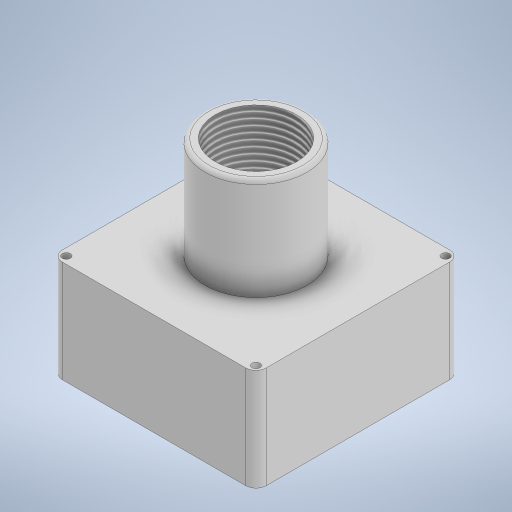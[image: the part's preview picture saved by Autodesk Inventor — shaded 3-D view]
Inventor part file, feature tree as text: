
AUTODESK INVENTOR PART (.ipt)
format: ipt  version: 2024 (Build 280153000, 153)  size: 256,512 bytes
history: native  units: in
note: dims shown in document units (in); Inventor stores cm internally (conversion verified against a paired STEP export)
features: extrude x3, sketch x3, thread x1, fillet x1
ambient origin geometry x8: Origin, YZ Plane, XZ Plane, XY Plane, X Axis, Y Axis, Z Axis, Center Point
bodies: Solid1 (feature_tree)
feature tree (8):
  extrude  "Extrusion1"  Depth=3.937in
  extrude  "Extrusion2"  Depth=1.9685in TaperAngle=0.0deg
  extrude  "Extrusion3"  Depth=1.1811in TaperAngle=0.0deg
  thread  "Thread1"  [1 undecoded]
  fillet  "Fillet1"  Radius=0.0787in
  sketch  "Sketch1"  dims[d0=3.937in d1=3.937in]
  sketch  "Sketch2"  dims[d13=1.9685in d14=0.0in d16=1.9685in d17=0.0in]
  sketch  "Sketch3"  dims[d18=1.5748in d19=1.1811in d20=0.0in d21=1.1811in d22=0.0in d23=0.0787in d15=0.0197in]
note: 1 required parameter value undecoded (feature->parameter linkage not recoverable at this tier; creation-order binding heuristic only, values carry confidence <= 0.55)
